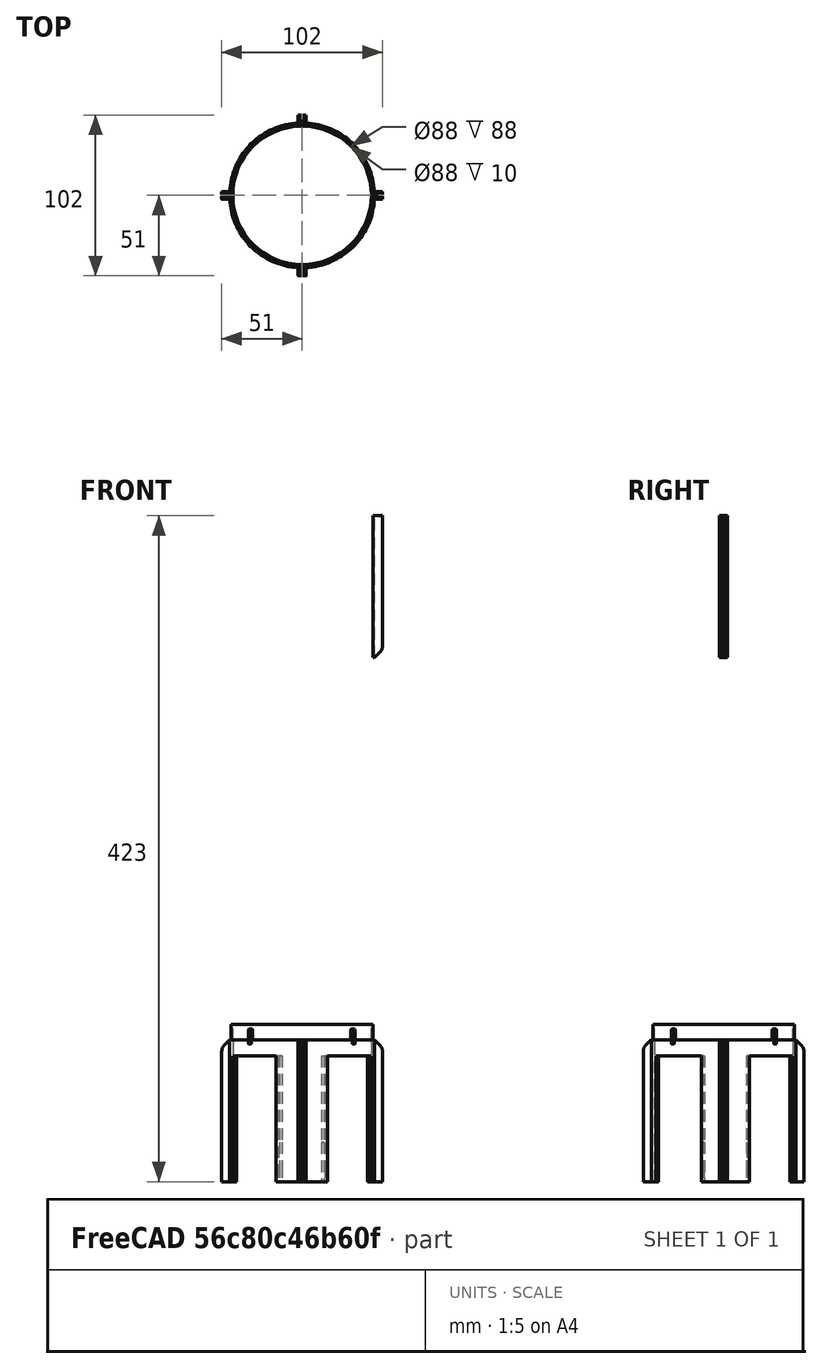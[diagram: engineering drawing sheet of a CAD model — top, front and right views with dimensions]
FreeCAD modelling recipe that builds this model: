
FCSTD DOCUMENT  (FreeCAD 1.0R39109 (Git))
Label: Faldon
License: All rights reserved
LicenseURL: http://en.wikipedia.org/wiki/All_rights_reserved
objects: Part::Box×10, Part::Fillet×10, Part::Chamfer×5, Part::Cut×4, Part::MultiFuse×4, Part::FeaturePython×3
note: 35 computed .brp shape members not serialized (recipe doc carries the construction recipe); baked Part::Feature solids carry a one-line shape summary decoded from their .brp

FEATURE [Part::Box] Box362  label="Cubo345"
  AttacherType = Attacher::AttachEngine3D
  Height = 90
  Length = 6
  Placement = pos=(45,-2.5,0) rot=(0,0,1;0rad)
  Width = 5
FEATURE [Part::Box] Box363  label="Cubo346"
  AttacherType = Attacher::AttachEngine3D
  Height = 100
  Length = 10
  Placement = pos=(46,-0.5,0) rot=(0,0,1;0rad)
  Width = 1
FEATURE [Part::Box] Box364  label="Cubo347"
  AttacherType = Attacher::AttachEngine3D
  Height = 70
  Length = 100
  Placement = pos=(-23,-50,10) rot=(0,0,1;0.785398rad)
  Width = 40
FEATURE [Part::Box] Box365  label="Cubo348"
  AttacherType = Attacher::AttachEngine3D
  Height = 70
  Length = 100
  Placement = pos=(50,-20,10) rot=(0,0,1;2.35619rad)
  Width = 40
FEATURE [Part::Box] Box366  label="Cubo349"
  AttacherType = Attacher::AttachEngine3D
  Height = 10
  Length = 2
  Placement = pos=(-32.5,-34,47) rot=(0,0,1;0.785398rad)
  Width = 3
FEATURE [Part::Box] Box367  label="Cubo350"
  AttacherType = Attacher::AttachEngine3D
  Height = 10
  Length = 2
  Placement = pos=(-32.5,-34,47) rot=(0,0,1;0.785398rad)
  Width = 3
FEATURE [Part::Box] Box368  label="Cubo351"
  AttacherType = Attacher::AttachEngine3D
  Height = 10
  Length = 2
  Placement = pos=(-32.5,-34,47) rot=(0,0,1;0.785398rad)
  Width = 3
FEATURE [Part::Box] Box369  label="Cubo352"
  AttacherType = Attacher::AttachEngine3D
  Height = 10
  Length = 2
  Placement = pos=(-32.5,-34,47) rot=(0,0,1;0.785398rad)
  Width = 3
FEATURE [Part::Box] Box370  label="Cubo353"
  AttacherType = Attacher::AttachEngine3D
  Height = 30
  Length = 101
  Placement = pos=(-47,20,-338) rot=(0,0,-1;0.785398rad)
  Width = 40
FEATURE [Part::Box] Box371  label="Cubo354"
  AttacherType = Attacher::AttachEngine3D
  Height = 30
  Length = 101
  Placement = pos=(-24,-50.5,-338) rot=(0,0,1;0.785398rad)
  Width = 40
FEATURE [Part::Cut] Cut361
  Base = -> Box362
  Tool = -> Box363
FEATURE [Part::Chamfer] Chamfer053
  Base = -> Cut361
  EdgeLinks = -> Cut361 [Edge16,Edge20]
  Edges = 2 edges r=5: [Edge16,Edge20]
FEATURE [Part::Fillet] Fillet247  label="SoporteAla001"
  Base = -> Chamfer053
  EdgeLinks = -> Chamfer053 [Edge12,Edge25]
  Edges = 2 edges r=5: [Edge12,Edge25]
FEATURE [Part::FeaturePython] Array024  # Draft array (typed FeaturePython)
  AlwaysSyncPlacement = false
  Angle = 360
  ArrayType = 1
  Axis = (0,0,1)
  Base = -> Fillet247
  Center = (0,0,0)
  Count = 4
  ExpandArray = false
  Fuse = false
  IntervalAxis = (0,0,0)
  IntervalX = (50,0,0)
  IntervalY = (0,50,0)
  IntervalZ = (0,0,50)
  NumberCircles = 3
  NumberPolar = 4
  NumberX = 2
  NumberY = 2
  NumberZ = 1
  PlacementList = 4 placements: [(0,0,0),(0,0,0),(0,0,0),(0,0,0)]
  RadialDistance = 50
  ScaleList = (4) [(1,1,1),(1,1,1),(1,1,1),(1,1,1)]
  Symmetry = 1
  TangentialDistance = 25
FEATURE [Part::Fillet] Fillet249
  Base = -> Box366
  EdgeLinks = -> Box366 [Edge10,Edge12]
  Edges = 2 edges r=0.8: [Edge10,Edge12]
FEATURE [Part::Fillet] Fillet250
  Base = -> Fillet249
  EdgeLinks = -> Fillet249 [Edge8,Edge12]
  Edges = 2 edges r=0.8: [Edge8,Edge12]
FEATURE [Part::Chamfer] Chamfer054
  Base = -> Fillet250
  EdgeLinks = -> Fillet250 [Edge1,Edge5]
  Edges = 2 edges r=0.7: [Edge1,Edge5]
  Placement = pos=(0,1,0) rot=(0,0,1;0rad)
FEATURE [Part::Fillet] Fillet251
  Base = -> Box367
  EdgeLinks = -> Box367 [Edge10,Edge12]
  Edges = 2 edges r=0.8: [Edge10,Edge12]
FEATURE [Part::Fillet] Fillet252
  Base = -> Fillet251
  EdgeLinks = -> Fillet251 [Edge8,Edge12]
  Edges = 2 edges r=0.8: [Edge8,Edge12]
FEATURE [Part::Chamfer] Chamfer055
  Base = -> Fillet252
  EdgeLinks = -> Fillet252 [Edge1,Edge5]
  Edges = 2 edges r=0.7: [Edge1,Edge5]
  Placement = pos=(0,1,0) rot=(0,0,1;1.5708rad)
FEATURE [Part::Fillet] Fillet253
  Base = -> Box368
  EdgeLinks = -> Box368 [Edge10,Edge12]
  Edges = 2 edges r=0.8: [Edge10,Edge12]
FEATURE [Part::Fillet] Fillet254
  Base = -> Fillet253
  EdgeLinks = -> Fillet253 [Edge8,Edge12]
  Edges = 2 edges r=0.8: [Edge8,Edge12]
FEATURE [Part::Chamfer] Chamfer056
  Base = -> Fillet254
  EdgeLinks = -> Fillet254 [Edge1,Edge5]
  Edges = 2 edges r=0.7: [Edge1,Edge5]
  Placement = pos=(-1,0,0) rot=(0,0,1;3.14159rad)
FEATURE [Part::Fillet] Fillet255
  Base = -> Box369
  EdgeLinks = -> Box369 [Edge10,Edge12]
  Edges = 2 edges r=0.8: [Edge10,Edge12]
FEATURE [Part::Fillet] Fillet256
  Base = -> Fillet255
  EdgeLinks = -> Fillet255 [Edge8,Edge12]
  Edges = 2 edges r=0.8: [Edge8,Edge12]
FEATURE [Part::Chamfer] Chamfer057
  Base = -> Fillet256
  EdgeLinks = -> Fillet256 [Edge1,Edge5]
  Edges = 2 edges r=0.7: [Edge1,Edge5]
  Placement = pos=(0,-1,0) rot=(0,0,-1;1.5708rad)
FEATURE [Part::MultiFuse] Fusion231  label="Hueco001"
  Shapes = -> [Box364,Box365]
FEATURE [Part::FeaturePython] Tube020  # WARN: FeaturePython — macro-defined, semantics opaque (R4)
  AttacherType = Attacher::AttachEngine3D
  Height = 90
  InnerRadius = 44
  OuterRadius = 46
FEATURE [Part::Fillet] Fillet248
  Base = -> Tube020
  EdgeLinks = -> Tube020 [Edge3]
  Edges = 1 edges r=1: [Edge3]
FEATURE [Part::Cut] Cut362  label="FaldonSinSoporte001"
  Base = -> Fillet248
  Tool = -> Fusion231
FEATURE [Part::MultiFuse] Fusion232  label="Faldón001"
  Placement = pos=(0,0,50) rot=(0,1,0;3.14159rad)
  Shapes = -> [Cut362,Array024]
FEATURE [Part::FeaturePython] Tube021  # WARN: FeaturePython — macro-defined, semantics opaque (R4)
  AttacherType = Attacher::AttachEngine3D
  Height = 12
  InnerRadius = 44
  OuterRadius = 45
  Placement = pos=(0,0,48) rot=(0,0,1;0rad)
FEATURE [Part::MultiFuse] Fusion233  label="ExtraFaldon001"
  Shapes = -> [Tube021,Chamfer054,Chamfer055,Chamfer056,Chamfer057]
FEATURE [Part::MultiFuse] Fusion234  label="Faldon_Copia"
  Placement = pos=(0,0,-293) rot=(0,0,1;0rad)
  Shapes = -> [Fusion232,Fusion233]
FEATURE [Part::Cut] Cut363
  Base = -> Fusion234
  Tool = -> Box370
FEATURE [Part::Cut] Cut364  label="Faldon_Abierto"
  Base = -> Cut363
  Tool = -> Box371
